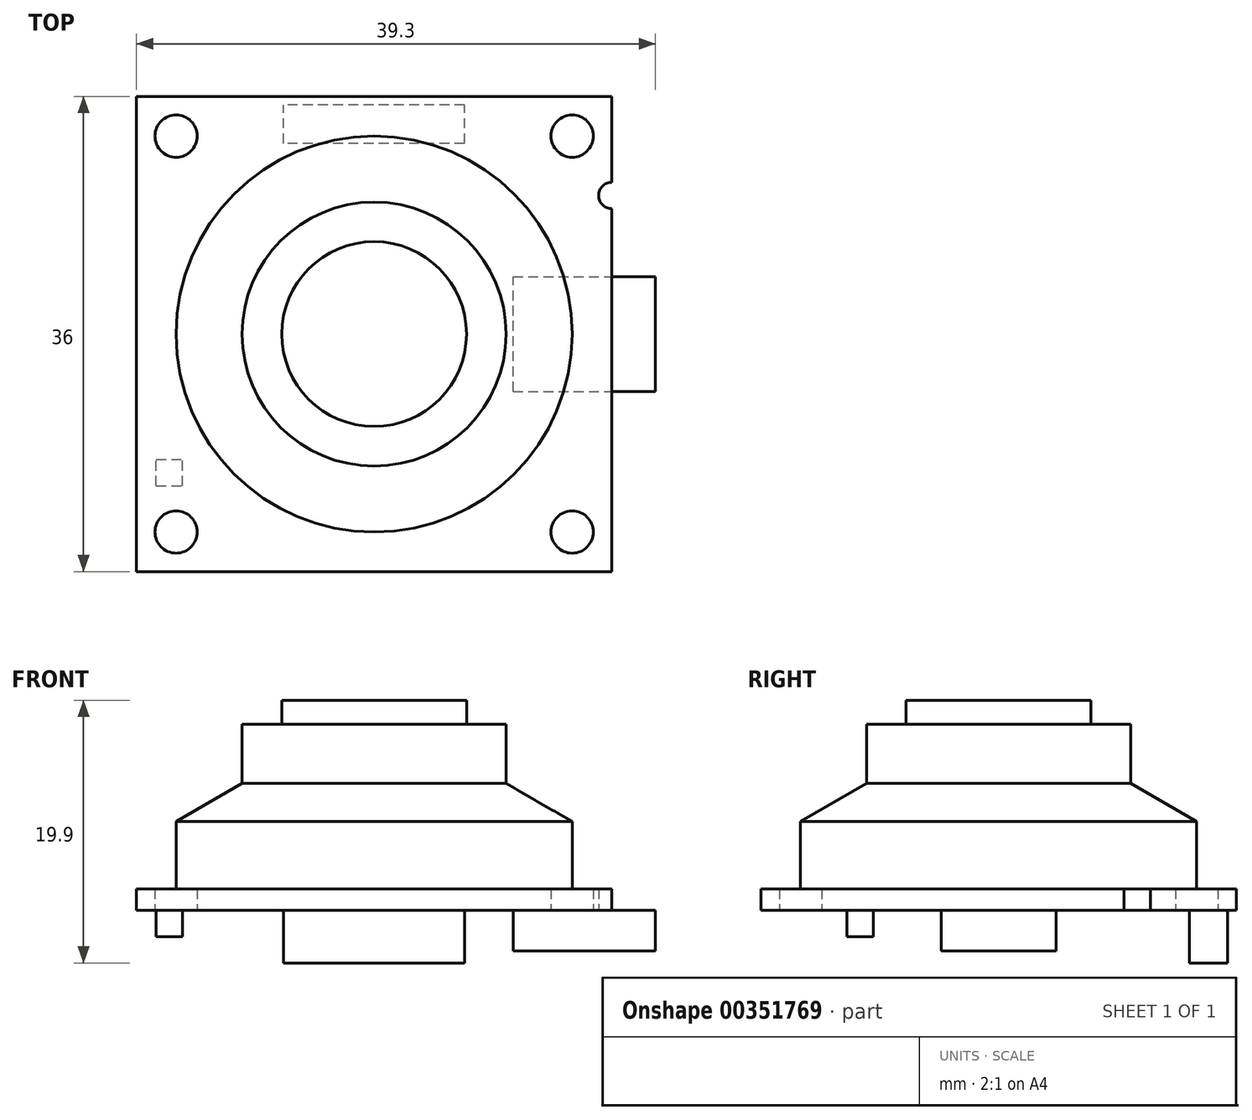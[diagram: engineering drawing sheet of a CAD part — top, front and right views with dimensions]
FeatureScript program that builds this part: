
annotation { "Feature Type Name" : "Feature", "Feature Type Description" : "" }
export const myFeature = defineFeature(function(context is Context, id is Id, definition is map)
    precondition{}
    {
        {
            var Q0;
            Q0=qCreatedBy(makeId("Top.planeOp"),FACE);
            var sketch = newSketch(context, id + "F0", { "sketchPlane" : qUnion([Q0])});
            skLineSegment(sketch, "E0.bottom", {"start": v(18, -18) * mm, "end": v(-18, -18) * mm});
            skLineSegment(sketch, "E0.top", {"start": v(18, 18) * mm, "end": v(-18, 18) * mm});
            skLineSegment(sketch, "E0.left", {"start": v(18, -18) * mm, "end": v(18, 18) * mm});
            skLineSegment(sketch, "E0.right", {"start": v(-18, -18) * mm, "end": v(-18, 18) * mm});
            skPoint(sketch, "E0.middle", {"position": v(0, 0) * mm});
            skCircle(sketch, "E1", {"center": v(-15, 15) * mm, "radius": 1.6 * mm});
            skCircle(sketch, "E2", {"center": v(15, 15) * mm, "radius": 1.6 * mm});
            skCircle(sketch, "E3", {"center": v(15, -15) * mm, "radius": 1.6 * mm});
            skCircle(sketch, "E4", {"center": v(-15, -15) * mm, "radius": 1.6 * mm});
            skLineSegment(sketch, "E5.bottom", {"start": v(6.85, 14.45) * mm, "end": v(-6.85, 14.45) * mm});
            skLineSegment(sketch, "E5.top", {"start": v(6.85, 17.35) * mm, "end": v(-6.85, 17.35) * mm});
            skLineSegment(sketch, "E5.left", {"start": v(6.85, 14.45) * mm, "end": v(6.85, 17.35) * mm});
            skLineSegment(sketch, "E5.right", {"start": v(-6.85, 14.45) * mm, "end": v(-6.85, 17.35) * mm});
            skPoint(sketch, "E5.middle", {"position": v(0, 15.9) * mm});
            skLineSegment(sketch, "E6.bottom", {"start": v(10.52, -4.35) * mm, "end": v(21.3, -4.35) * mm});
            skLineSegment(sketch, "E6.top", {"start": v(10.52, 4.35) * mm, "end": v(21.3, 4.35) * mm});
            skLineSegment(sketch, "E6.left", {"start": v(10.52, -4.35) * mm, "end": v(10.52, 4.35) * mm});
            skLineSegment(sketch, "E6.right", {"start": v(21.3, -4.35) * mm, "end": v(21.3, 4.35) * mm});
            skPoint(sketch, "E6.middle", {"position": v(15.91, 0) * mm});
            skCircle(sketch, "E7", {"center": v(18, 10.5) * mm, "radius": 1 * mm});
            skLineSegment(sketch, "E8.bottom", {"start": v(-16.5, -11.5) * mm, "end": v(-14.5, -11.5) * mm});
            skLineSegment(sketch, "E8.top", {"start": v(-16.5, -9.5) * mm, "end": v(-14.5, -9.5) * mm});
            skLineSegment(sketch, "E8.left", {"start": v(-16.5, -11.5) * mm, "end": v(-16.5, -9.5) * mm});
            skLineSegment(sketch, "E8.right", {"start": v(-14.5, -11.5) * mm, "end": v(-14.5, -9.5) * mm});
            skPoint(sketch, "E8.middle", {"position": v(-15.5, -10.5) * mm});
            skSolve(sketch);
        }
        {
            var Q0;
            Q0=makeQuery(id+"F0.imprint","IMPRINT",FACE,{"disambiguationData":[TD([[makeQuery(id+"F0.imprint","IMPRINT",EDGE,{"derivedFrom":sQuery(id+"F0.wireOp",EDGE,"E0.bottom")}),-1.0]])]});
            var Q1;
            Q1=makeQuery(id+"F0.imprint","IMPRINT",FACE,{"disambiguationData":[TD([[makeQuery(id+"F0.imprint","IMPRINT",EDGE,{"derivedFrom":sQuery(id+"F0.wireOp",EDGE,"E5.bottom")}),-1.0]])]});
            var Q2;
            Q2=makeQuery(id+"F0.imprint","IMPRINT",FACE,{"disambiguationData":[TD([[makeQuery(id+"F0.imprint","IMPRINT",EDGE,{"derivedFrom":sQuery(id+"F0.wireOp",EDGE,"E8.bottom")}),1.0]])]});
            var Q3;
            {var subQ5=sQuery(id+"F0.wireOp",EDGE,"E6.left");Q3=makeQuery(id+"F0.imprint","IMPRINT",FACE,{"disambiguationData":[TD([[makeQuery(id+"F0.imprint","IMPRINT",EDGE,{"derivedFrom":subQ5}),-1.0]])]});}
            extrude(context, id + "F1", {"entities" : qUnion([Q0, Q1, Q2, Q3]), "depth" : 1.6 * mm, "offsetDistance" : 25 * mm});
        }
        {
            var Q0;
            Q0=makeQuery(id+"F0.imprint","IMPRINT",FACE,{"disambiguationData":[TD([[makeQuery(id+"F0.imprint","IMPRINT",EDGE,{"derivedFrom":sQuery(id+"F0.wireOp",EDGE,"E5.bottom")}),-1.0]])]});
            extrude(context, id + "F2", {"entities" : qUnion([Q0]), "operationType" : NewBodyOperationType.ADD, "oppositeDirection" : true, "depth" : 4 * mm, "offsetDistance" : 25 * mm});
        }
        {
            var Q0;
            {var subQ5=sQuery(id+"F0.wireOp",EDGE,"E6.right");Q0=makeQuery(id+"F0.imprint","IMPRINT",FACE,{"disambiguationData":[TD([[makeQuery(id+"F0.imprint","IMPRINT",EDGE,{"derivedFrom":subQ5}),1.0]])]});}
            var Q1;
            {var subQ5=sQuery(id+"F0.wireOp",EDGE,"E6.left");Q1=makeQuery(id+"F0.imprint","IMPRINT",FACE,{"disambiguationData":[TD([[makeQuery(id+"F0.imprint","IMPRINT",EDGE,{"derivedFrom":subQ5}),-1.0]])]});}
            extrude(context, id + "F3", {"entities" : qUnion([Q0, Q1]), "operationType" : NewBodyOperationType.ADD, "oppositeDirection" : true, "depth" : 3.1 * mm, "offsetDistance" : 25 * mm});
        }
        {
            var Q0;
            Q0=makeQuery(id+"F0.imprint","IMPRINT",FACE,{"disambiguationData":[TD([[makeQuery(id+"F0.imprint","IMPRINT",EDGE,{"derivedFrom":sQuery(id+"F0.wireOp",EDGE,"E8.bottom")}),1.0]])]});
            extrude(context, id + "F4", {"entities" : qUnion([Q0]), "operationType" : NewBodyOperationType.ADD, "oppositeDirection" : true, "depth" : 2 * mm, "offsetDistance" : 25 * mm});
        }
        {
            var Q0;
            Q0=makeQuery(id+"F1.opExtrude","CAP_FACE",FACE,{"disambiguationData":[OSD([sQuery(id+"F0.wireOp",EDGE,"E0.bottom"),sQuery(id+"F0.wireOp",EDGE,"E0.top"),sQuery(id+"F0.wireOp",EDGE,"E0.left"),sQuery(id+"F0.wireOp",EDGE,"E0.right"),sQuery(id+"F0.wireOp",EDGE,"E1"),sQuery(id+"F0.wireOp",EDGE,"E2"),sQuery(id+"F0.wireOp",EDGE,"E3"),sQuery(id+"F0.wireOp",EDGE,"E4"),sQuery(id+"F0.wireOp",EDGE,"E7")])],"isStart":false});
            var sketch = newSketch(context, id + "F5", { "sketchPlane" : qUnion([Q0])});
            skCircle(sketch, "E9", {"center": v(0, 0) * mm, "radius": 15 * mm});
            skCircle(sketch, "E10", {"center": v(0, 0) * mm, "radius": 10 * mm});
            skCircle(sketch, "E11", {"center": v(0, 0) * mm, "radius": 7 * mm});
            skSolve(sketch);
        }
        {
            var Q0;
            Q0=makeQuery(id+"F5.imprint","IMPRINT",FACE,{"disambiguationData":[TD([[makeQuery(id+"F5.imprint","IMPRINT",EDGE,{"derivedFrom":sQuery(id+"F5.wireOp",EDGE,"E9")}),1.0]])]});
            extrude(context, id + "F6", {"entities" : qUnion([Q0]), "operationType" : NewBodyOperationType.ADD, "depth" : 8 * mm, "offsetDistance" : 25 * mm});
        }
        {
            var Q0;
            Q0=makeQuery(id+"F6.boolean.opBoolean","SPLIT",FACE,{"disambiguationData":[TD([makeQuery(id+"F6.opExtrude","SWEPT_FACE",FACE,{"disambiguationData":[OSD([sQuery(id+"F5.wireOp",EDGE,"E10")])]})])],"derivedFrom":makeQuery(id+"F1.opExtrude","CAP_FACE",FACE,{"disambiguationData":[OSD([sQuery(id+"F0.wireOp",EDGE,"E0.bottom"),sQuery(id+"F0.wireOp",EDGE,"E0.top"),sQuery(id+"F0.wireOp",EDGE,"E0.left"),sQuery(id+"F0.wireOp",EDGE,"E0.right"),sQuery(id+"F0.wireOp",EDGE,"E1"),sQuery(id+"F0.wireOp",EDGE,"E2"),sQuery(id+"F0.wireOp",EDGE,"E3"),sQuery(id+"F0.wireOp",EDGE,"E4"),sQuery(id+"F0.wireOp",EDGE,"E7")])],"isStart":false})});
            extrude(context, id + "F7", {"entities" : qUnion([Q0]), "operationType" : NewBodyOperationType.ADD, "depth" : 12.5 * mm, "offsetDistance" : 25 * mm});
        }
        {
            var Q0;
            Q0=makeQuery(id+"F6.opExtrude","CAP_EDGE",EDGE,{"disambiguationData":[OSD([sQuery(id+"F5.wireOp",EDGE,"E9")])],"isStart":false});
            chamfer(context, id + "F8", {"entities" : qUnion([Q0]), "chamferType" : ChamferType.OFFSET_ANGLE, "width" : 5 * mm, "oppositeDirection" : false, "angle" : 30 * degree, "tangentPropagation" : true});
        }
        {
            var Q0;
            Q0=makeQuery(id+"F5.imprint","IMPRINT",FACE,{"disambiguationData":[TD([[makeQuery(id+"F5.imprint","IMPRINT",EDGE,{"derivedFrom":sQuery(id+"F5.wireOp",EDGE,"E11")}),1.0]])]});
            extrude(context, id + "F9", {"entities" : qUnion([Q0]), "operationType" : NewBodyOperationType.ADD, "depth" : 14.3 * mm, "offsetDistance" : 25 * mm});
        }
    });
